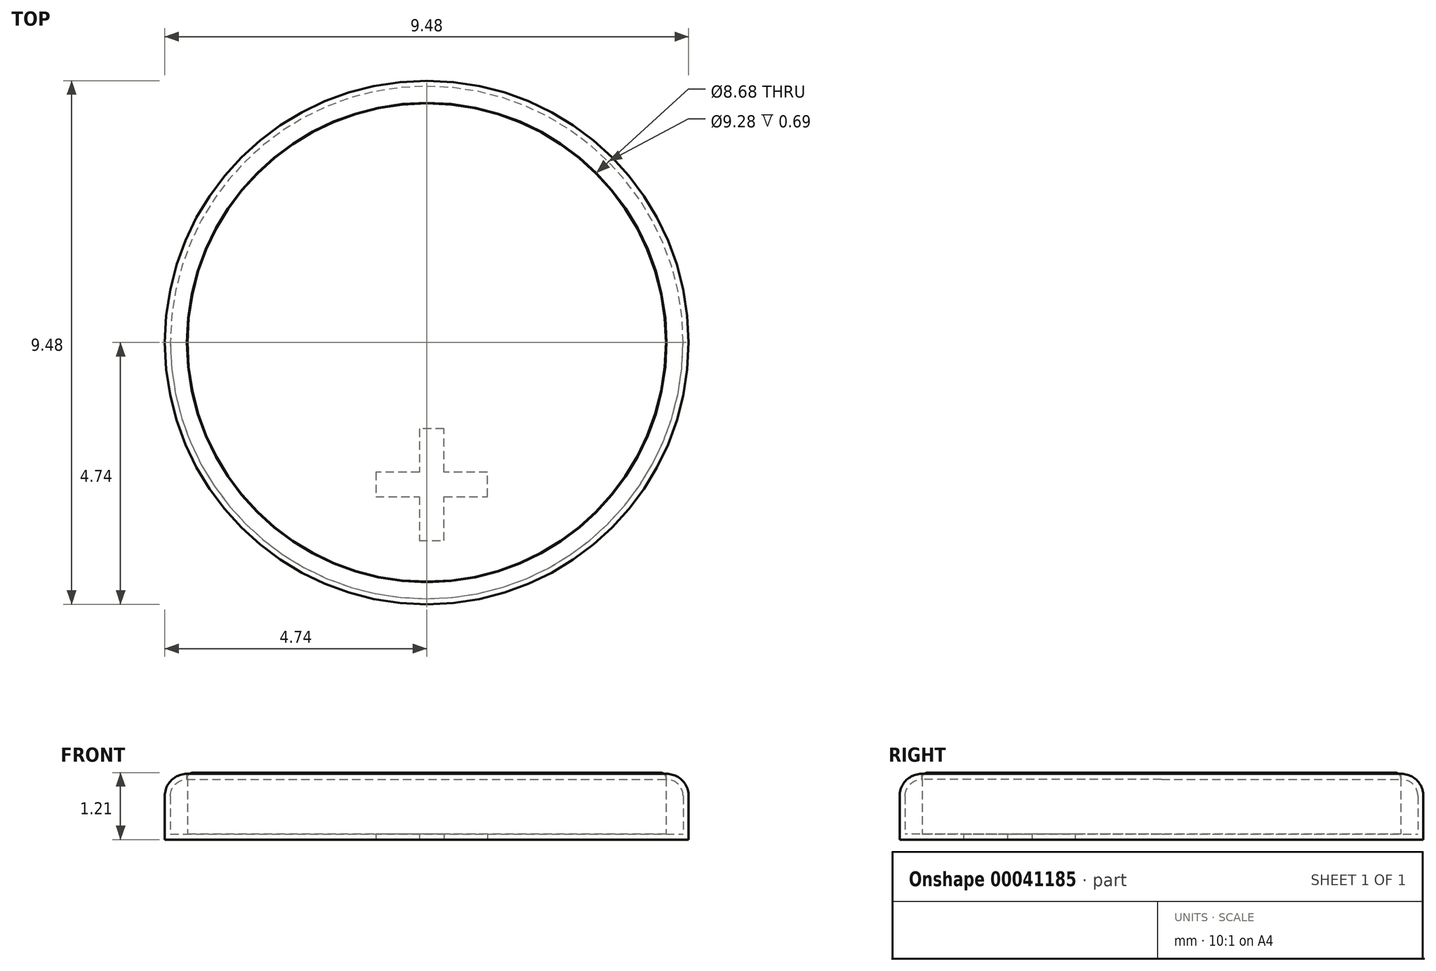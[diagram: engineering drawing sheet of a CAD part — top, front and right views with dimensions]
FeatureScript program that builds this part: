
annotation { "Feature Type Name" : "Feature", "Feature Type Description" : "" }
export const myFeature = defineFeature(function(context is Context, id is Id, definition is map)
    precondition{}
    {
        {
            var Q0;
            Q0=qCreatedBy(makeId("Top.planeOp"),FACE);
            var sketch = newSketch(context, id + "F0", { "sketchPlane" : qUnion([Q0])});
            skCircle(sketch, "E0", {"center": v(0, 0) * mm, "radius": 4.74 * mm});
            skSolve(sketch);
        }
        {
            var Q0;
            Q0 = qSketchRegion(id + "F0", true);
            extrude(context, id + "F1", {"entities" : qUnion([Q0]), "depth" : 1.19 * mm});
        }
        {
            var Q0;
            Q0=makeQuery(id+"F1.opExtrude","CAP_EDGE",EDGE,{"disambiguationData":[OSD([sQuery(id+"F0.wireOp",EDGE,"E0")])],"isStart":false});
            fillet(context, id + "F2", {"entities" : qUnion([Q0]), "radius" : .4 * mm, "tangentPropagation" : true, "allowEdgeOverflow" : false});
        }
        {
            var Q0;
            Q0=makeQuery(id+"F1.opExtrude","CAP_FACE",FACE,{"disambiguationData":[OSD([sQuery(id+"F0.wireOp",EDGE,"E0")])],"isStart":false});
            var Q1;
            Q1=makeQuery(id+"F1.opExtrude","SWEPT_BODY",BODY,{"disambiguationData":[OSD([sQuery(id+"F0.wireOp",EDGE,"E0")])]});
            shell(context, id + "F3", {"entities" : qUnion([Q0]), "parts" : qUnion([Q1]), "thickness" : .1 * mm});
        }
        {
            var Q0;
            {var subQ0=sQuery(id+"F0.wireOp",EDGE,"E0");Q0=makeQuery(id+"F3.opShell","OFFSET_FACE",FACE,{"disambiguationData":[OSD([subQ0]),TDD([makeQuery(id+"F1.opExtrude","CAP_FACE",FACE,{"disambiguationData":[OSD([subQ0])],"isStart":true})])]});}
            var sketch = newSketch(context, id + "F4", { "sketchPlane" : qUnion([Q0])});
            skCircle(sketch, "E1", {"center": v(0, 0) * mm, "radius": 4.3 * mm, "construction": true});
            skCircle(sketch, "E2", {"center": v(0, 0) * mm, "radius": 4.33 * mm});
            skSolve(sketch);
        }
        {
            var Q0;
            Q0 = qSketchRegion(id + "F4", true);
            extrude(context, id + "F5", {"entities" : qUnion([Q0]), "operationType" : NewBodyOperationType.ADD, "depth" : 1.11 * mm});
        }
        {
            var Q0;
            Q0=makeQuery(id+"F5.opExtrude","CAP_EDGE",EDGE,{"disambiguationData":[OSD([sQuery(id+"F4.wireOp",EDGE,"E2")])],"isStart":false});
            fillet(context, id + "F6", {"entities" : qUnion([Q0]), "radius" : .1 * mm, "tangentPropagation" : true, "allowEdgeOverflow" : false});
        }
        {
            var Q0;
            Q0=makeQuery(id+"F1.opExtrude","CAP_FACE",FACE,{"disambiguationData":[OSD([sQuery(id+"F0.wireOp",EDGE,"E0")])],"isStart":true});
            var sketch = newSketch(context, id + "F7", { "sketchPlane" : qUnion([Q0])});
            skText(sketch, "E3", { "text": "+", "fontName": "OpenSans-Bold.ttf"});
            skLineSegment(sketch, "E4", {"start": v(-1.1, 2.6) * mm, "end": v(1.1, 2.6) * mm, "construction": true});
            const initialGuessF7  = {"E3": [-0.0011, 0.0011, 1, 0, 0.003]};
            skSetInitialGuess(sketch, initialGuessF7);
            skSolve(sketch);
        }
        {
            var Q0;
            Q0 = qSketchRegion(id + "F7", true);
            extrude(context, id + "F8", {"entities" : qUnion([Q0]), "operationType" : NewBodyOperationType.REMOVE, "oppositeDirection" : true, "depth" : .1 * mm});
        }
    });
